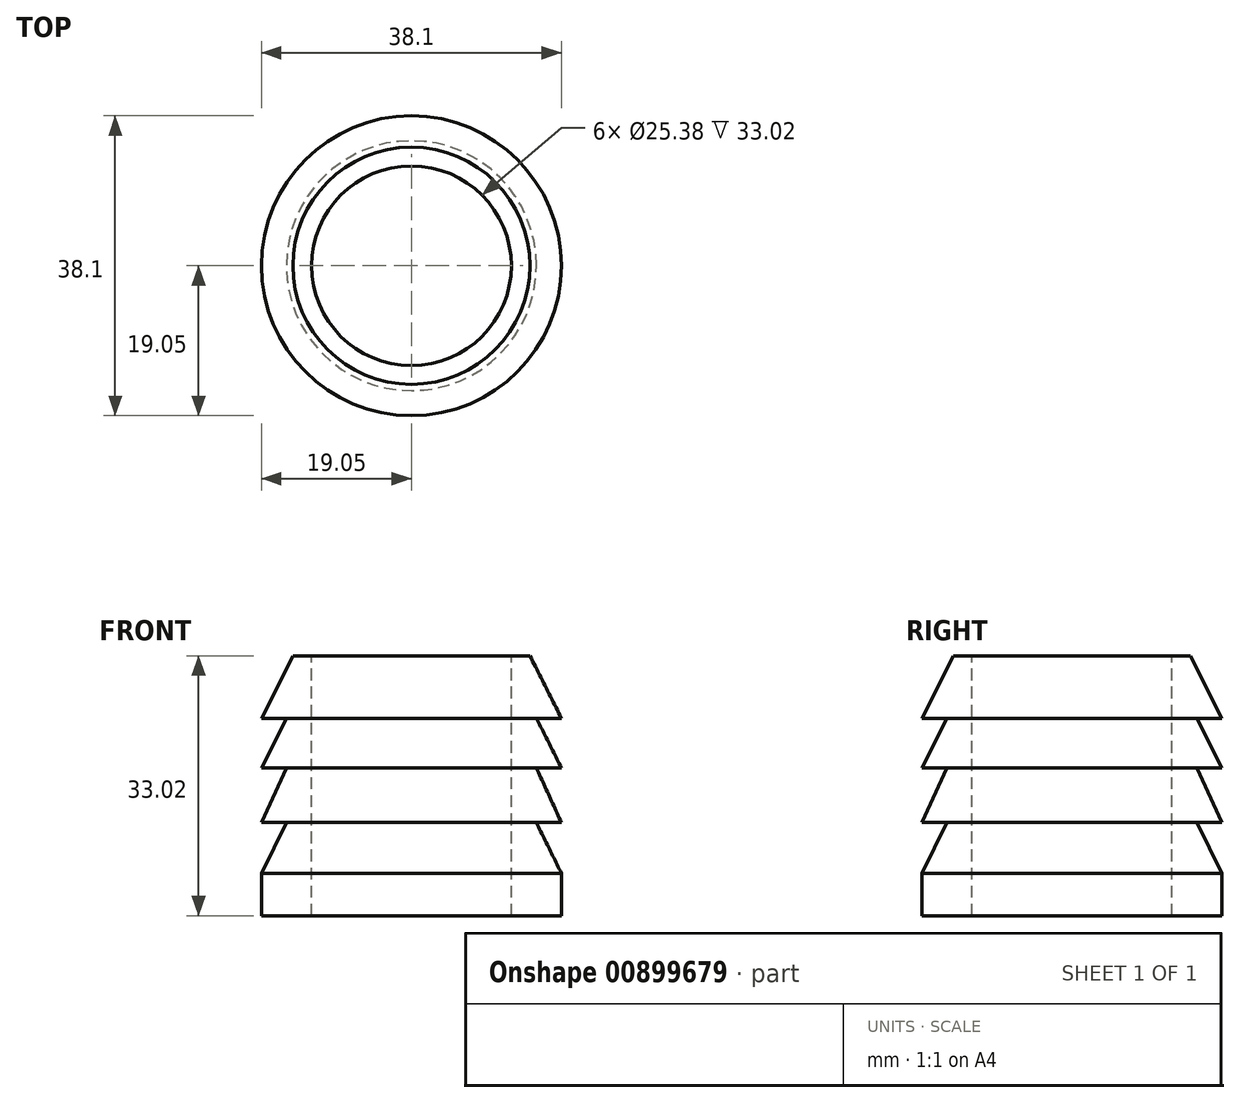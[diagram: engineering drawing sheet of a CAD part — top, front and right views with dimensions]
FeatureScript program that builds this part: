
annotation { "Feature Type Name" : "Feature", "Feature Type Description" : "" }
export const myFeature = defineFeature(function(context is Context, id is Id, definition is map)
    precondition{}
    {
        {
            var Q0;
            Q0=qCreatedBy(makeId("Front.planeOp"),FACE);
            var sketch = newSketch(context, id + "F0", { "sketchPlane" : qUnion([Q0])});
            skLineSegment(sketch, "E0", {"start": v(0, 0) * mm, "end": v(19.05, 0) * mm});
            skLineSegment(sketch, "E1", {"start": v(19.05, 0) * mm, "end": v(19.05, 5.39) * mm});
            skLineSegment(sketch, "E2", {"start": v(19.05, 5.39) * mm, "end": v(15.88, 11.82) * mm});
            skLineSegment(sketch, "E3", {"start": v(15.88, 11.82) * mm, "end": v(19.05, 11.82) * mm});
            skLineSegment(sketch, "E4", {"start": v(19.05, 11.82) * mm, "end": v(15.88, 18.79) * mm});
            skLineSegment(sketch, "E5", {"start": v(15.88, 18.79) * mm, "end": v(19.05, 18.79) * mm});
            skLineSegment(sketch, "E6", {"start": v(19.05, 18.79) * mm, "end": v(15.88, 25.1) * mm});
            skLineSegment(sketch, "E7", {"start": v(15.88, 25.1) * mm, "end": v(19.05, 25.1) * mm});
            skLineSegment(sketch, "E8", {"start": v(19.05, 25.1) * mm, "end": v(15.06, 33.02) * mm});
            skLineSegment(sketch, "E9", {"start": v(15.06, 33.02) * mm, "end": v(0, 33.02) * mm});
            skLineSegment(sketch, "E10", {"start": v(0, 33.02) * mm, "end": v(0, 0) * mm});
            skSolve(sketch);
        }
        {
            var Q0;
            Q0=makeQuery(id+"F0.imprint","IMPRINT",FACE,{"disambiguationData":[TD([[makeQuery(id+"F0.imprint","IMPRINT",EDGE,{"derivedFrom":sQuery(id+"F0.wireOp",EDGE,"E0")}),1.0]])]});
            var Q1;
            Q1=sQuery(id+"F0.wireOp",EDGE,"E10");
            revolve(context, id + "F1", {"surfaceOperationType" : NewSurfaceOperationType.NEW, "entities" : qUnion([Q0]), "axis" : qUnion([Q1]), "revolveType" : RevolveType.FULL});
        }
        {
            var Q0;
            Q0=makeQuery(id+"F1.opRevolve","SWEPT_FACE",FACE,{"disambiguationData":[OSD([sQuery(id+"F0.wireOp",EDGE,"E9")])]});
            var sketch = newSketch(context, id + "F2", { "sketchPlane" : qUnion([Q0])});
            skCircle(sketch, "E11", {"center": v(0, 0) * mm, "radius": 12.69 * mm});
            skSolve(sketch);
        }
        {
            var Q0;
            Q0=makeQuery(id+"F2.imprint","IMPRINT",FACE,{"disambiguationData":[TD([[makeQuery(id+"F2.imprint","IMPRINT",EDGE,{"derivedFrom":sQuery(id+"F2.wireOp",EDGE,"E11")}),1.0]])]});
            var Q1;
            Q1=makeQuery(id+"F1.opRevolve","SWEPT_FACE",FACE,{"disambiguationData":[OSD([sQuery(id+"F0.wireOp",EDGE,"E0")])]});
            extrude(context, id + "F3", {"entities" : qUnion([Q0]), "operationType" : NewBodyOperationType.REMOVE, "endBound" : BoundingType.UP_TO_SURFACE, "oppositeDirection" : true, "depth" : 25.4 * mm, "endBoundEntityFace" : qUnion([Q1]), "offsetDistance" : 25.4 * mm});
        }
    });
